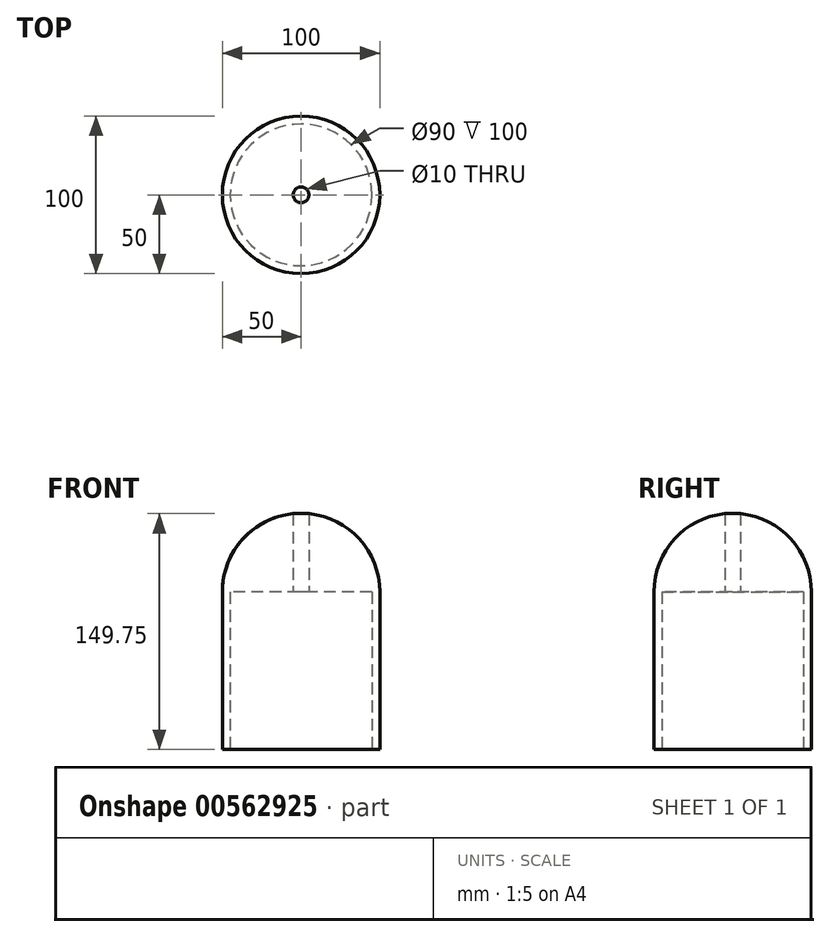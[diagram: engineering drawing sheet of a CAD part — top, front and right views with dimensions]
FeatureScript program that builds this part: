
annotation { "Feature Type Name" : "Feature", "Feature Type Description" : "" }
export const myFeature = defineFeature(function(context is Context, id is Id, definition is map)
    precondition{}
    {
        {
            var Q0;
            Q0=qCreatedBy(makeId("Front.planeOp"),FACE);
            var sketch = newSketch(context, id + "F0", { "sketchPlane" : qUnion([Q0])});
            skLineSegment(sketch, "E0.bottom", {"start": v(0, 0) * mm, "end": v(-50, 0) * mm});
            skLineSegment(sketch, "E0.top", {"start": v(0, 150) * mm, "end": v(0, 150) * mm});
            skLineSegment(sketch, "E0.left", {"start": v(0, 0) * mm, "end": v(0, 150) * mm});
            skLineSegment(sketch, "E0.right", {"start": v(-50, 0) * mm, "end": v(-50, 100) * mm});
            skPoint(sketch, "E1.visualSharp", {"position": v(-50, 150) * mm});
            skArc(sketch, "E1.filletArc", {"start": v(0, 150) * mm, "mid": v(-35.36, 135.36) * mm, "end": v(-50, 100) * mm});
            skSolve(sketch);
        }
        {
            var Q0;
            Q0=qSketchRegion(id+"F0",true);
            var Q1;
            Q1=sQuery(id+"F0.wireOp",EDGE,"E0.left");
            revolve(context, id + "F1", {"entities" : qUnion([Q0]), "axis" : qUnion([Q1]), "revolveType" : RevolveType.FULL});
        }
        {
            var Q0;
            Q0=qCreatedBy(makeId("Top.planeOp"),FACE);
            var sketch = newSketch(context, id + "F2", { "sketchPlane" : qUnion([Q0])});
            skCircle(sketch, "E2", {"center": v(0, 0) * mm, "radius": 45 * mm});
            skSolve(sketch);
        }
        {
            var Q0;
            Q0=qSketchRegion(id+"F2",true);
            extrude(context, id + "F3", {"entities" : qUnion([Q0]), "operationType" : NewBodyOperationType.REMOVE, "depth" : 100 * mm, "offsetDistance" : 25 * mm});
        }
        {
            var Q0;
            Q0=qCreatedBy(makeId("Top.planeOp"),FACE);
            var sketch = newSketch(context, id + "F4", { "sketchPlane" : qUnion([Q0])});
            skCircle(sketch, "E3", {"center": v(0, 0) * mm, "radius": 5 * mm});
            skSolve(sketch);
        }
        {
            var Q0;
            Q0=qSketchRegion(id+"F4",true);
            extrude(context, id + "F5", {"entities" : qUnion([Q0]), "operationType" : NewBodyOperationType.REMOVE, "endBound" : BoundingType.THROUGH_ALL, "depth" : 25 * mm, "offsetDistance" : 25 * mm});
        }
    });
